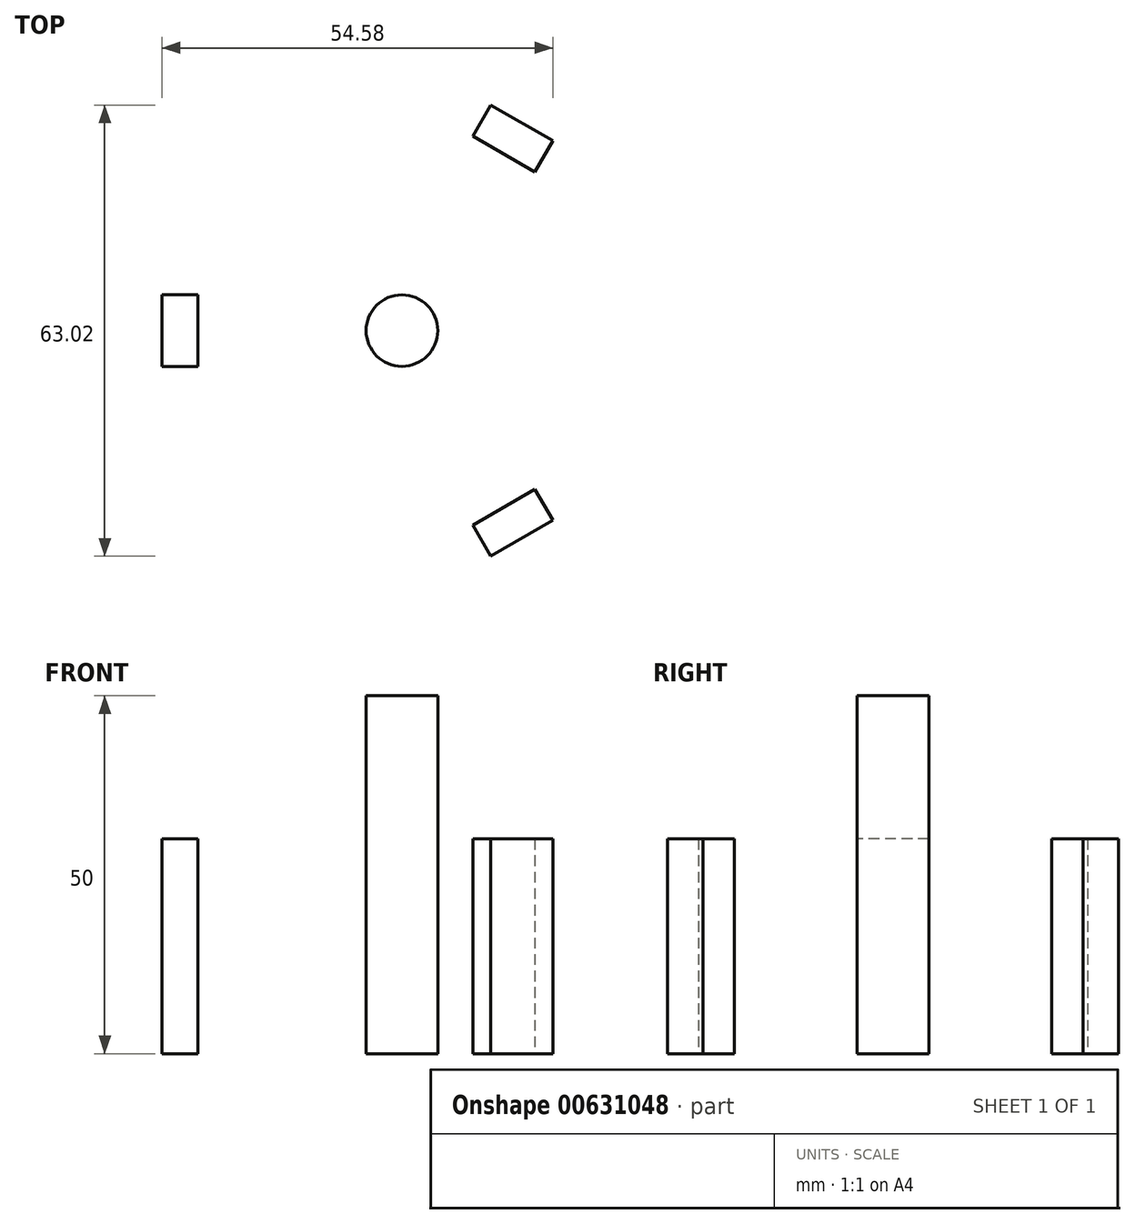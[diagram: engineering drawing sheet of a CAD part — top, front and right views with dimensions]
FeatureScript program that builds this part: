
annotation { "Feature Type Name" : "Feature", "Feature Type Description" : "" }
export const myFeature = defineFeature(function(context is Context, id is Id, definition is map)
    precondition{}
    {
        {
            var Q0;
            Q0=qCreatedBy(makeId("Top.planeOp"),FACE);
            var sketch = newSketch(context, id + "F0", { "sketchPlane" : qUnion([Q0])});
            skCircle(sketch, "E0.cCircle", {"center": v(0, 0) * mm, "radius": 28.5 * mm, "construction": true});
            skLineSegment(sketch, "E0.0", {"start": v(-28.5, 0) * mm, "end": v(14.25, 24.68) * mm});
            skLineSegment(sketch, "E0.1", {"start": v(14.25, 24.68) * mm, "end": v(14.25, -24.68) * mm});
            skLineSegment(sketch, "E0.2", {"start": v(14.25, -24.68) * mm, "end": v(-28.5, 0) * mm});
            skLineSegment(sketch, "E1.bottom", {"start": v(-28.5, 5) * mm, "end": v(-33.5, 5) * mm});
            skLineSegment(sketch, "E1.top", {"start": v(-28.5, -5) * mm, "end": v(-33.5, -5) * mm});
            skLineSegment(sketch, "E1.left", {"start": v(-28.5, 5) * mm, "end": v(-28.5, -5) * mm});
            skLineSegment(sketch, "E1.right", {"start": v(-33.5, 5) * mm, "end": v(-33.5, -5) * mm});
            skPoint(sketch, "E1.middle", {"position": v(-31, 0) * mm});
            skLineSegment(sketch, "E2.1.0", {"start": v(9.92, -27.18) * mm, "end": v(12.42, -31.51) * mm});
            skLineSegment(sketch, "E2.1.1", {"start": v(12.42, -31.51) * mm, "end": v(21.08, -26.51) * mm});
            skLineSegment(sketch, "E2.1.2", {"start": v(18.58, -22.18) * mm, "end": v(21.08, -26.51) * mm});
            skLineSegment(sketch, "E2.1.3", {"start": v(9.92, -27.18) * mm, "end": v(18.58, -22.18) * mm});
            skLineSegment(sketch, "E2.2.0", {"start": v(18.58, 22.18) * mm, "end": v(21.08, 26.51) * mm});
            skLineSegment(sketch, "E2.2.1", {"start": v(21.08, 26.51) * mm, "end": v(12.42, 31.51) * mm});
            skLineSegment(sketch, "E2.2.2", {"start": v(9.92, 27.18) * mm, "end": v(12.42, 31.51) * mm});
            skLineSegment(sketch, "E2.2.3", {"start": v(18.58, 22.18) * mm, "end": v(9.92, 27.18) * mm});
            skCircle(sketch, "E3", {"center": v(0, 0) * mm, "radius": 5 * mm});
            skSolve(sketch);
        }
        {
            var Q0;
            {var subQ2=sQuery(id+"F0.wireOp",EDGE,"E2.1.0");Q0=makeQuery(id+"F0.imprint","IMPRINT",FACE,{"disambiguationData":[TD([[makeQuery(id+"F0.imprint","IMPRINT",EDGE,{"derivedFrom":subQ2}),1.0]])]});}
            var Q1;
            {var subQ2=sQuery(id+"F0.wireOp",EDGE,"E2.2.0");Q1=makeQuery(id+"F0.imprint","IMPRINT",FACE,{"disambiguationData":[TD([[makeQuery(id+"F0.imprint","IMPRINT",EDGE,{"derivedFrom":subQ2}),1.0]])]});}
            var Q2;
            {var subQ3=sQuery(id+"F0.wireOp",EDGE,"E1.bottom");Q2=makeQuery(id+"F0.imprint","IMPRINT",FACE,{"disambiguationData":[TD([[makeQuery(id+"F0.imprint","IMPRINT",EDGE,{"derivedFrom":subQ3}),1.0]])]});}
            extrude(context, id + "F1", {"entities" : qUnion([Q0, Q1, Q2]), "depth" : 30 * mm, "offsetDistance" : 25 * mm});
        }
        {
            var Q0;
            Q0=makeQuery(id+"F0.imprint","IMPRINT",FACE,{"disambiguationData":[TD([[makeQuery(id+"F0.imprint","IMPRINT",EDGE,{"derivedFrom":sQuery(id+"F0.wireOp",EDGE,"E3")}),1.0]])]});
            extrude(context, id + "F2", {"entities" : qUnion([Q0]), "depth" : 50 * mm, "offsetDistance" : 25 * mm});
        }
    });
